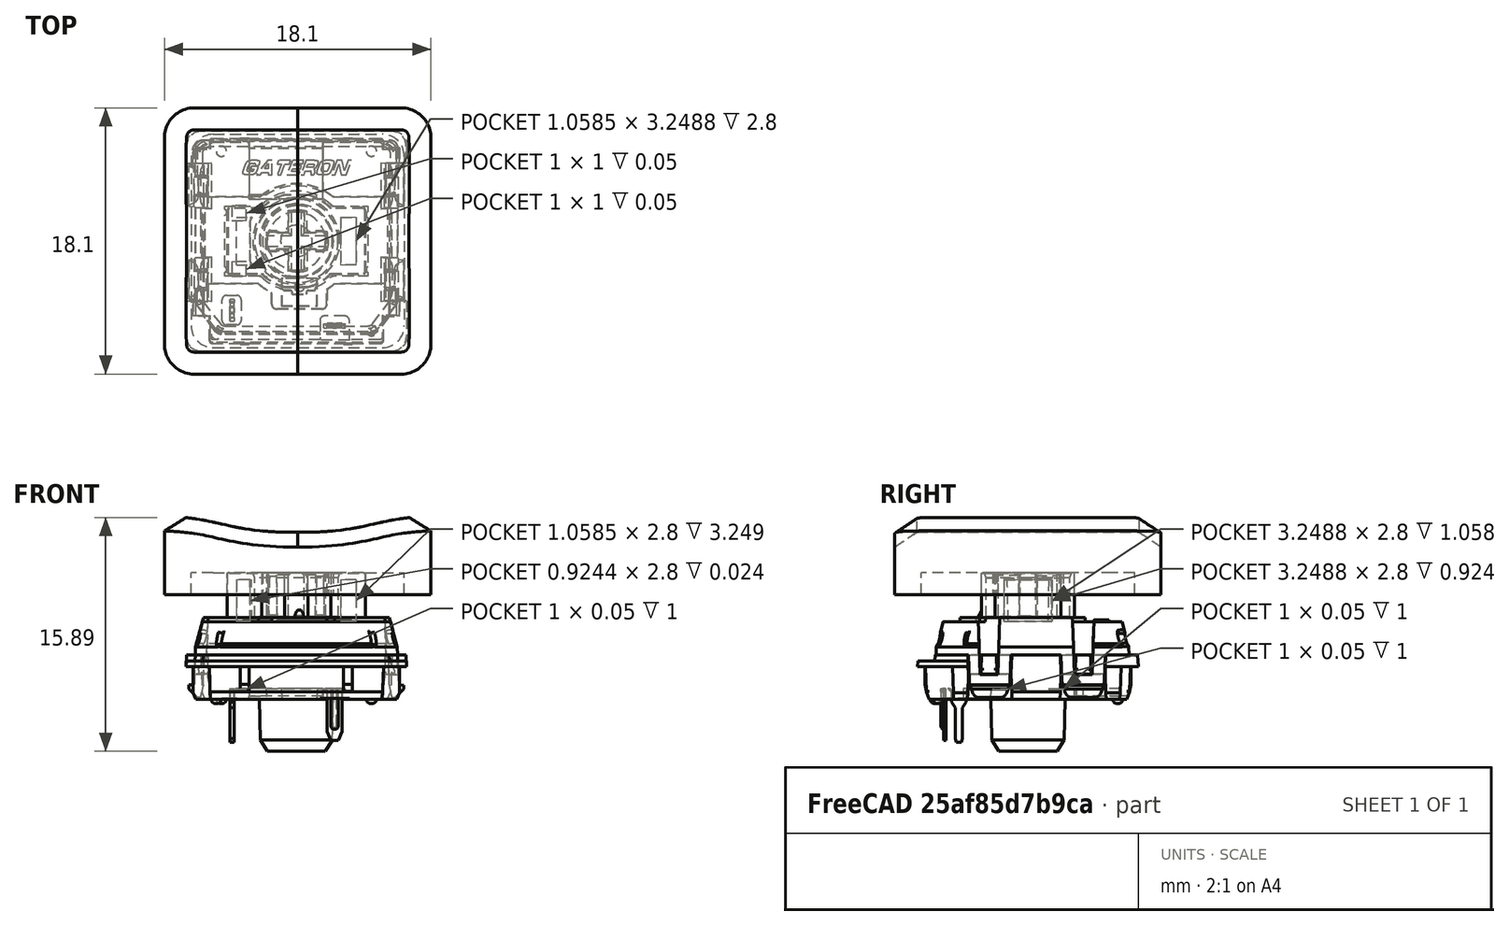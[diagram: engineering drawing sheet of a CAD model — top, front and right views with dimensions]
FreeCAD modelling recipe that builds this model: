
FCSTD DOCUMENT  (FreeCAD 0.21R33771 (Git))
Label: switch_keycap
License: All rights reserved
LicenseURL: https://en.wikipedia.org/wiki/All_rights_reserved
objects: App::FeaturePython×6, Part::FeaturePython×2, Sketcher::SketchObject×1, PartDesign::Body×1
note: 4 computed .brp shape members not serialized (recipe doc carries the construction recipe); baked Part::Feature solids carry a one-line shape summary decoded from their .brp

FEATURE [Part::FeaturePython] b_KS_33_Low_Profile_2_0__KS33_20230109_xef_xbc_x88KS_33_Y31__3D_xe5_x9b_xbe_xef_xbc_x891_001_  label="KS-33 Low Profile 2.0  KS33-20230109（KS-33-Y31  3D图）1_001"  # a2plus imported part (geometry in sourceFile) (typed FeaturePython)
  a2p_Version = 0.4.65
  fixedPosition = true
  objectType = a2pPart
  sourceFile = .\..\Design\PCBA-LOW-PROFILE-SWITCH\KS-33 Low Profile 2.0  KS33-20230109（KS-33-Y31  3D图）.stp
  subassemblyImport = false
  timeLastImport = 1.68656e+09
  updateColors = true
FEATURE [Part::FeaturePython] b_PLASTIC_LOW_PROFILE_KEYCAP_THT_001_  label="PLASTIC-LOW-PROFILE-KEYCAP_THT_001"  # a2plus imported part (geometry in sourceFile) (typed FeaturePython)
  Placement = pos=(60.09,-2.1273e-12,10.65) rot=(0,0,1;0rad)
  a2p_Version = 0.4.65
  fixedPosition = false
  objectType = a2pPart
  sourceFile = .\..\Design\PLASTIC-LOW-PROFILE-KEYCAP\PLASTIC-LOW-PROFILE-KEYCAP_THT.FCStd
  subassemblyImport = false
  timeLastImport = 1.74029e+09
  updateColors = true
FEATURE [App::FeaturePython] planeCoincident_001  label="planeCoincident_001__KS-33 Low Profile 2.0  KS33-20230109（KS-33-Y31  3D图）1_001"  # a2plus constraint (typed FeaturePython)
  Object1 = b_PLASTIC_LOW_PROFILE_KEYCAP_THT_001_
  Object2 = b_KS_33_Low_Profile_2_0__KS33_20230109_xef_xbc_x88KS_33_Y31__3D_xe5_x9b_xbe_xef_xbc_x891_001_
  ParentTreeObject = -> b_PLASTIC_LOW_PROFILE_KEYCAP_THT_001_
  SubElement1 = Face43
  SubElement2 = Face606
  Suppressed = false
  Type = plane
  directionConstraint = 1
  offset = 0
FEATURE [App::FeaturePython] planeCoincident_001_mirror  label="planeCoincident_001__PLASTIC-LOW-PROFILE-KEYCAP_THT_001"  # a2plus constraint (typed FeaturePython)
  Object1 = b_PLASTIC_LOW_PROFILE_KEYCAP_THT_001_
  Object2 = b_KS_33_Low_Profile_2_0__KS33_20230109_xef_xbc_x88KS_33_Y31__3D_xe5_x9b_xbe_xef_xbc_x891_001_
  ParentTreeObject = -> b_KS_33_Low_Profile_2_0__KS33_20230109_xef_xbc_x88KS_33_Y31__3D_xe5_x9b_xbe_xef_xbc_x891_001_
  SubElement1 = Face43
  SubElement2 = Face606
  Suppressed = false
  Type = plane
  directionConstraint = 1
  offset = 0
FEATURE [App::FeaturePython] planeCoincident_002  label="planeCoincident_002__KS-33 Low Profile 2.0  KS33-20230109（KS-33-Y31  3D图）1_001"  # a2plus constraint (typed FeaturePython)
  Object1 = b_PLASTIC_LOW_PROFILE_KEYCAP_THT_001_
  Object2 = b_KS_33_Low_Profile_2_0__KS33_20230109_xef_xbc_x88KS_33_Y31__3D_xe5_x9b_xbe_xef_xbc_x891_001_
  ParentTreeObject = -> b_PLASTIC_LOW_PROFILE_KEYCAP_THT_001_
  SubElement1 = Face41
  SubElement2 = Face614
  Suppressed = false
  Type = plane
  directionConstraint = 0
  offset = 0
FEATURE [App::FeaturePython] planeCoincident_002_mirror  label="planeCoincident_002__PLASTIC-LOW-PROFILE-KEYCAP_THT_001"  # a2plus constraint (typed FeaturePython)
  Object1 = b_PLASTIC_LOW_PROFILE_KEYCAP_THT_001_
  Object2 = b_KS_33_Low_Profile_2_0__KS33_20230109_xef_xbc_x88KS_33_Y31__3D_xe5_x9b_xbe_xef_xbc_x891_001_
  ParentTreeObject = -> b_KS_33_Low_Profile_2_0__KS33_20230109_xef_xbc_x88KS_33_Y31__3D_xe5_x9b_xbe_xef_xbc_x891_001_
  SubElement1 = Face41
  SubElement2 = Face614
  Suppressed = false
  Type = plane
  directionConstraint = 0
  offset = 0
FEATURE [App::FeaturePython] planeCoincident_003  label="planeCoincident_003__KS-33 Low Profile 2.0  KS33-20230109（KS-33-Y31  3D图）1_001"  # a2plus constraint (typed FeaturePython)
  Object1 = b_PLASTIC_LOW_PROFILE_KEYCAP_THT_001_
  Object2 = b_KS_33_Low_Profile_2_0__KS33_20230109_xef_xbc_x88KS_33_Y31__3D_xe5_x9b_xbe_xef_xbc_x891_001_
  ParentTreeObject = -> b_PLASTIC_LOW_PROFILE_KEYCAP_THT_001_
  SubElement1 = Face38
  SubElement2 = Face644
  Suppressed = false
  Type = plane
  directionConstraint = 1
  offset = 0
FEATURE [App::FeaturePython] planeCoincident_003_mirror  label="planeCoincident_003__PLASTIC-LOW-PROFILE-KEYCAP_THT_001"  # a2plus constraint (typed FeaturePython)
  Object1 = b_PLASTIC_LOW_PROFILE_KEYCAP_THT_001_
  Object2 = b_KS_33_Low_Profile_2_0__KS33_20230109_xef_xbc_x88KS_33_Y31__3D_xe5_x9b_xbe_xef_xbc_x891_001_
  ParentTreeObject = -> b_KS_33_Low_Profile_2_0__KS33_20230109_xef_xbc_x88KS_33_Y31__3D_xe5_x9b_xbe_xef_xbc_x891_001_
  SubElement1 = Face38
  SubElement2 = Face644
  Suppressed = false
  Type = plane
  directionConstraint = 1
  offset = 0
FEATURE [Sketcher::SketchObject] Sketch
  FullyConstrained = true
  MapMode = 5
  Placement = pos=(0,0,0) rot=(1,0,0;1.5708rad)
  Support = -> [XZ_Plane]
FEATURE [PartDesign::Body] Body
  Group = -> [Sketch]
  Origin = -> Origin
